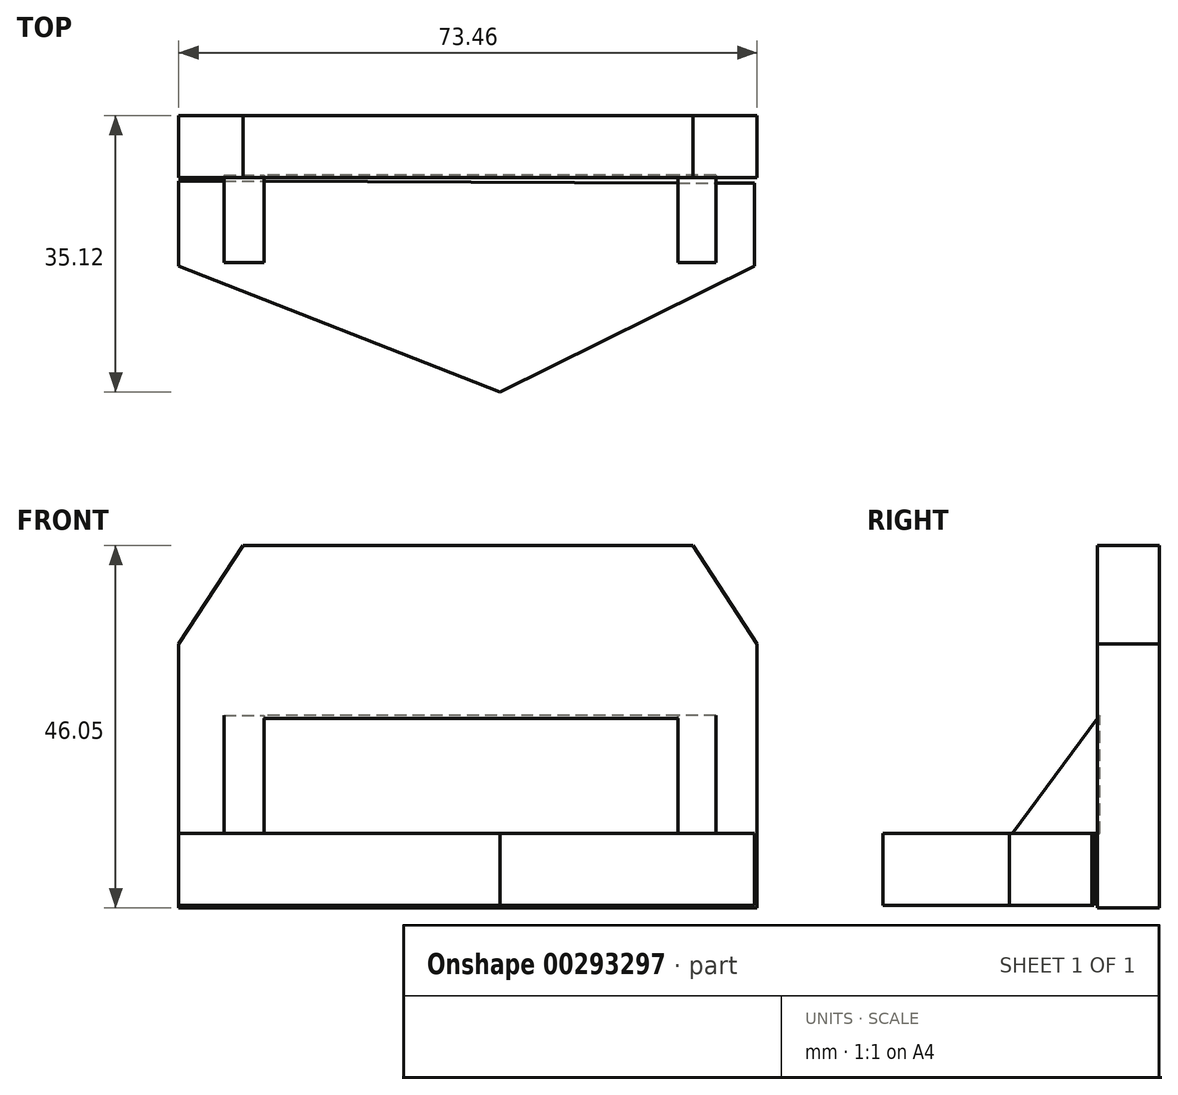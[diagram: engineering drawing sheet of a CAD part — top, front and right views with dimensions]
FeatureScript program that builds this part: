
annotation { "Feature Type Name" : "Feature", "Feature Type Description" : "" }
export const myFeature = defineFeature(function(context is Context, id is Id, definition is map)
    precondition{}
    {
        {
            var Q0;
            Q0=qCreatedBy(makeId("Front.planeOp"),FACE);
            var sketch = newSketch(context, id + "F0", { "sketchPlane" : qUnion([Q0])});
            skLineSegment(sketch, "E0", {"start": v(-32.65, 36.58) * mm, "end": v(24.48, 36.58) * mm});
            skLineSegment(sketch, "E1", {"start": v(24.48, 36.58) * mm, "end": v(32.65, 24.05) * mm});
            skLineSegment(sketch, "E2", {"start": v(32.65, 24.05) * mm, "end": v(24.48, 36.58) * mm});
            skLineSegment(sketch, "E3", {"start": v(-32.65, 36.58) * mm, "end": v(-40.8, 24.05) * mm});
            skLineSegment(sketch, "E4", {"start": v(-40.8, 24.05) * mm, "end": v(-32.65, 36.58) * mm});
            skLineSegment(sketch, "E5", {"start": v(-40.8, 24.05) * mm, "end": v(-40.8, -9.47) * mm});
            skLineSegment(sketch, "E6", {"start": v(-40.8, -9.47) * mm, "end": v(-40.8, 24.05) * mm});
            skLineSegment(sketch, "E7", {"start": v(32.65, 24.05) * mm, "end": v(32.65, -9.47) * mm});
            skLineSegment(sketch, "E8", {"start": v(32.65, -9.47) * mm, "end": v(32.65, 24.05) * mm});
            skLineSegment(sketch, "E9", {"start": v(-40.8, -9.47) * mm, "end": v(32.65, -9.47) * mm});
            skSolve(sketch);
        }
        {
            var Q0;
            Q0 = qSketchRegion(id + "F0", true);
            extrude(context, id + "F1", {"entities" : qUnion([Q0]), "depth" : 7.87 * mm});
        }
        {
            var Q0;
            Q0=qCreatedBy(makeId("Top.planeOp"),FACE);
            var sketch = newSketch(context, id + "F2", { "sketchPlane" : qUnion([Q0])});
            skLineSegment(sketch, "E10", {"start": v(-40.8, -8.3) * mm, "end": v(-40.8, -19.1) * mm});
            skLineSegment(sketch, "E11", {"start": v(-40.8, -19.1) * mm, "end": v(0, -35.12) * mm});
            skLineSegment(sketch, "E12", {"start": v(0, -35.12) * mm, "end": v(32.35, -19.1) * mm});
            skLineSegment(sketch, "E13", {"start": v(32.35, -19.1) * mm, "end": v(32.35, -8.6) * mm});
            skLineSegment(sketch, "E14", {"start": v(-40.8, -8.3) * mm, "end": v(32.35, -8.6) * mm});
            skSolve(sketch);
        }
        {
            var Q0;
            Q0 = qSketchRegion(id + "F2", true);
            extrude(context, id + "F3", {"entities" : qUnion([Q0]), "oppositeDirection" : true, "depth" : 9.14 * mm});
        }
        {
            var Q0;
            Q0=qCreatedBy(makeId("Right.planeOp"),FACE);
            var sketch = newSketch(context, id + "F4", { "sketchPlane" : qUnion([Q0])});
            skLineSegment(sketch, "E15", {"start": v(-7.58, 0) * mm, "end": v(-7.58, 15.01) * mm});
            skLineSegment(sketch, "E16", {"start": v(-7.58, 15.01) * mm, "end": v(-18.65, 0) * mm});
            skLineSegment(sketch, "E17", {"start": v(-18.65, 0) * mm, "end": v(-7.58, 0) * mm});
            skSolve(sketch);
        }
        {
            var Q0;
            Q0 = qSketchRegion(id + "F4", true);
            extrude(context, id + "F5", {"entities" : qUnion([Q0]), "depth" : 27.43 * mm});
        }
        {
            var Q0;
            Q0=makeQuery(id+"F5.opExtrude","CAP_FACE",FACE,{"disambiguationData":[OSD([sQuery(id+"F4.wireOp",EDGE,"E15"),sQuery(id+"F4.wireOp",EDGE,"E16"),sQuery(id+"F4.wireOp",EDGE,"E17")])],"isStart":true});
            extrude(context, id + "F6", {"entities" : qUnion([Q0]), "operationType" : NewBodyOperationType.REMOVE, "oppositeDirection" : true, "depth" : 22.6 * mm});
        }
        {
            var Q0;
            Q0 = qSketchRegion(id + "F4", true);
            extrude(context, id + "F7", {"entities" : qUnion([Q0]), "oppositeDirection" : true, "depth" : 35.05 * mm});
        }
        {
            var Q0;
            Q0=makeQuery(id+"F7.opExtrude","CAP_FACE",FACE,{"disambiguationData":[OSD([sQuery(id+"F4.wireOp",EDGE,"E15"),sQuery(id+"F4.wireOp",EDGE,"E16"),sQuery(id+"F4.wireOp",EDGE,"E17")])],"isStart":true});
            extrude(context, id + "F8", {"entities" : qUnion([Q0]), "operationType" : NewBodyOperationType.REMOVE, "oppositeDirection" : true, "depth" : 29.97 * mm});
        }
    });
